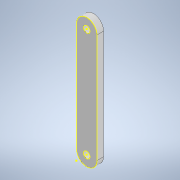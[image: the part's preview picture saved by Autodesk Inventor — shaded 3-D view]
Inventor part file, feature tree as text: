
AUTODESK INVENTOR PART (.ipt)
format: ipt  version: 2022 (Build 260153000, 153)  size: 114,688 bytes
history: native  units: mm
features: sketch x2, extrude x1, hole x1, fillet x1, projected_geometry x1
ambient origin geometry x8: Origin, YZ Plane, XZ Plane, XY Plane, X Axis, Y Axis, Z Axis, Center Point
bodies: Solid1 (feature_tree)
feature tree (6):
  sketch  "Sketch1"  dims[d0=50.8mm d3=9.525mm]
  extrude  "Extrusion1"  Depth=9.525mm
  hole  "Hole1"  [1 undecoded]
  fillet  "Fillet1"  [1 undecoded]
  sketch  "Sketch2"  dims[d4=3.175mm d5=0.0mm d6=3.0mm d7=6.0mm d8=4.0mm d9=2.0mm d10=90.0deg d11=8.0mm d12=20.594885mm d13=4.7625mm]
  projected_geometry  "Projected Loop1"
note: 2 required parameter values undecoded (feature->parameter linkage not recoverable at this tier; creation-order binding heuristic only, values carry confidence <= 0.55)
